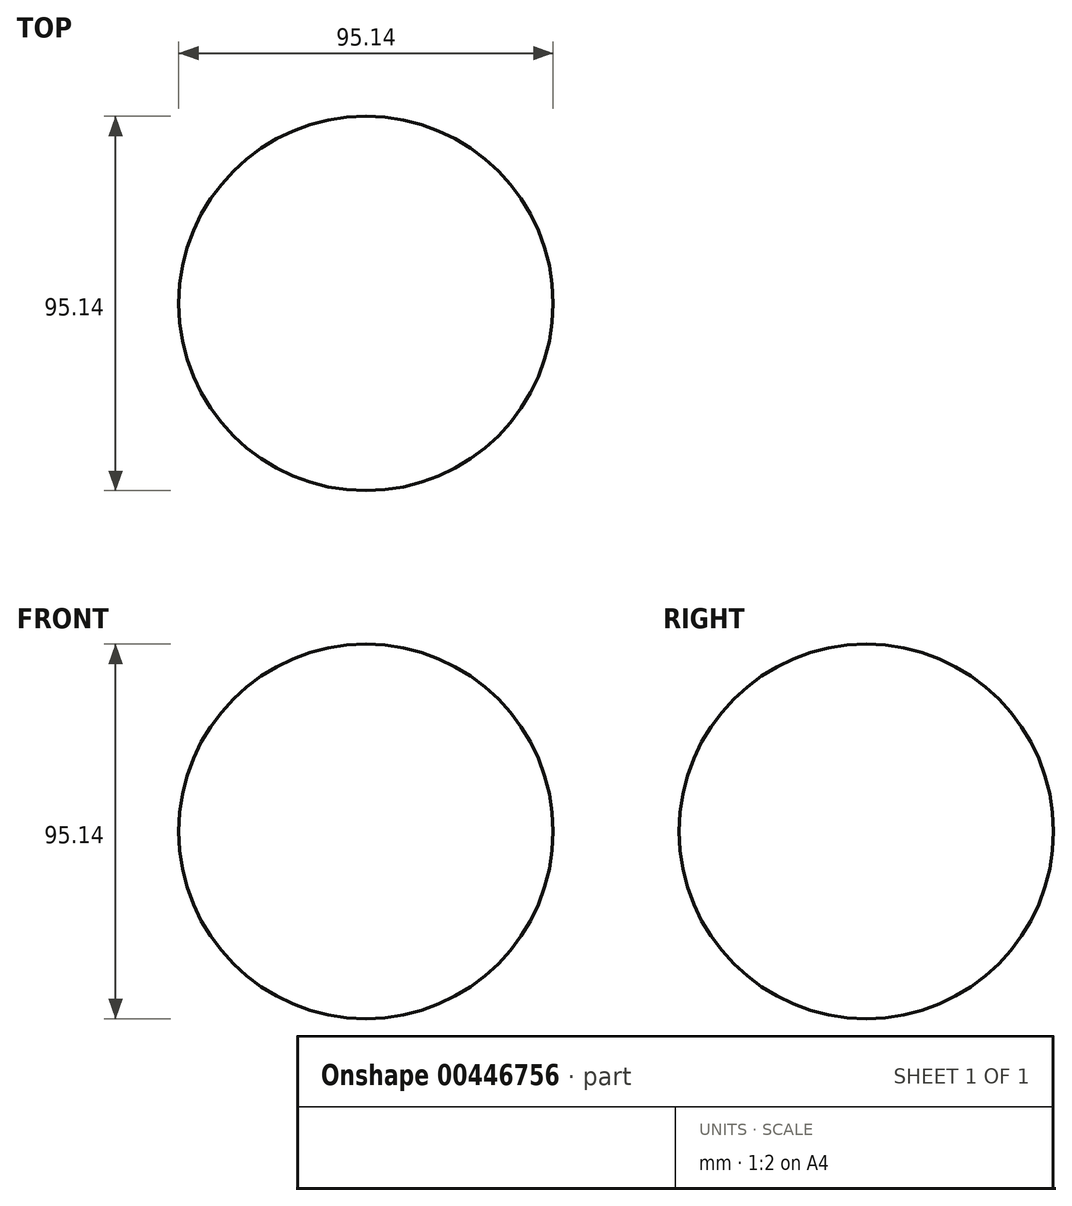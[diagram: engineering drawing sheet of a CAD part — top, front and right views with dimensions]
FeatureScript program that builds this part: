
annotation { "Feature Type Name" : "Feature", "Feature Type Description" : "" }
export const myFeature = defineFeature(function(context is Context, id is Id, definition is map)
    precondition{}
    {
        {
            var Q0;
            Q0=qCreatedBy(makeId("Front.planeOp"),FACE);
            var sketch = newSketch(context, id + "F0", { "sketchPlane" : qUnion([Q0])});
            skArc(sketch, "E0", {"start": v(0, -47.57) * mm, "mid": v(47.57, 0) * mm, "end": v(0, 47.57) * mm});
            skLineSegment(sketch, "E1", {"start": v(0, 47.57) * mm, "end": v(0, -47.57) * mm});
            skPoint(sketch, "E2.orphan", {"position": v(0, 52.83) * mm});
            skSolve(sketch);
        }
        {
            var Q0;
            Q0 = qSketchRegion(id + "F0", true);
            var Q1;
            Q1=sQuery(id+"F0.wireOp",EDGE,"E1");
            revolve(context, id + "F1", {"entities" : qUnion([Q0]), "axis" : qUnion([Q1]), "revolveType" : RevolveType.FULL});
        }
    });
